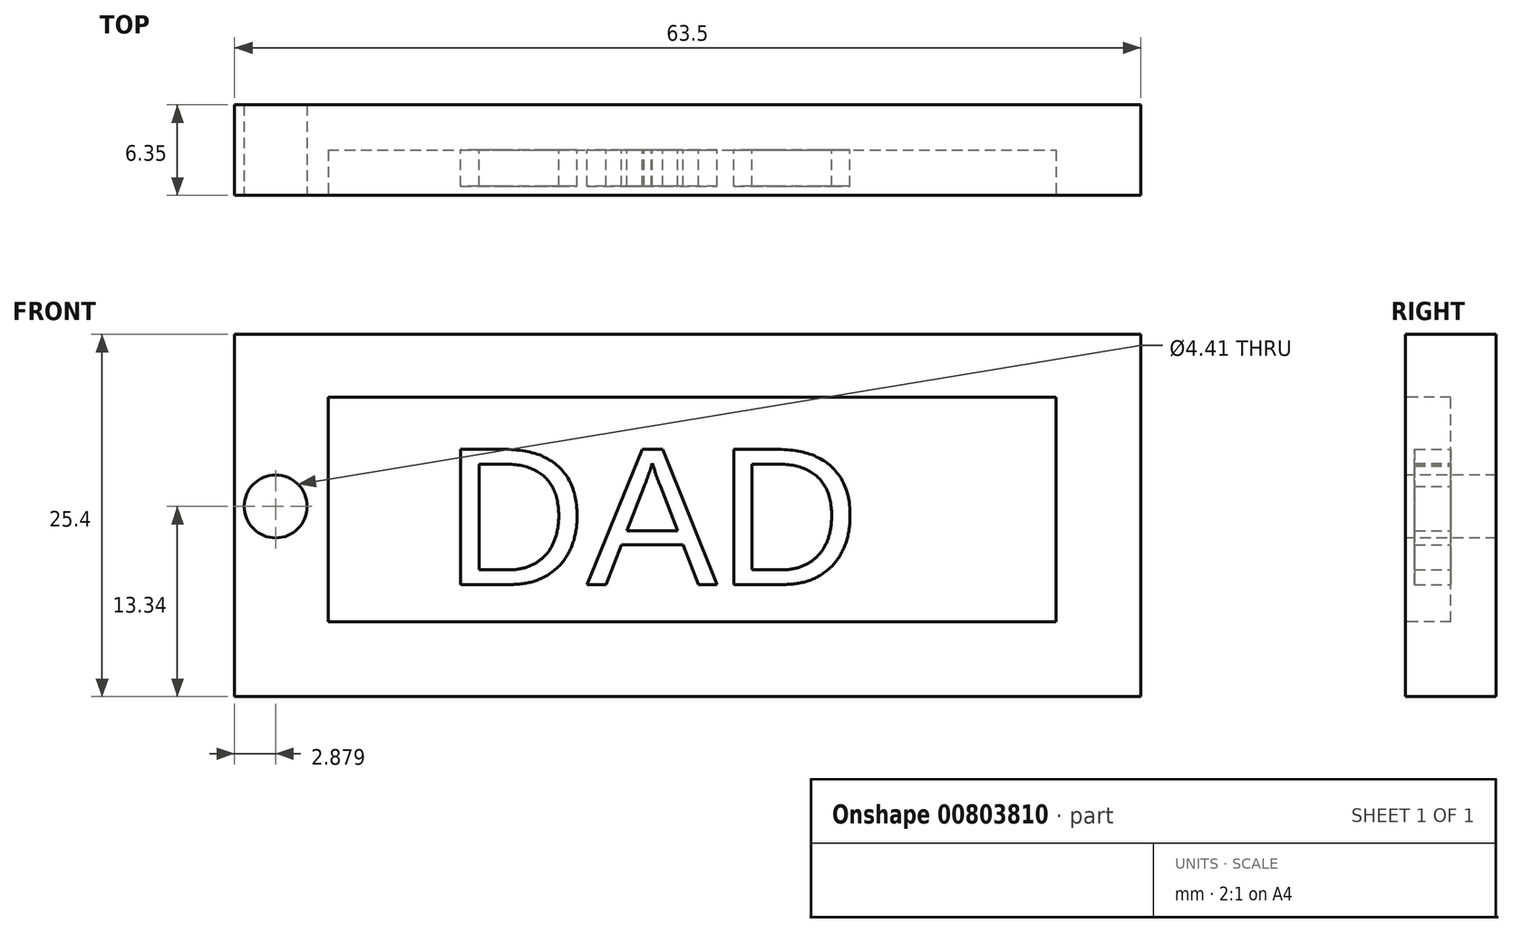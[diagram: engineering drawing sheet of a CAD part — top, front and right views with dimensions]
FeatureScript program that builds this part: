
annotation { "Feature Type Name" : "Feature", "Feature Type Description" : "" }
export const myFeature = defineFeature(function(context is Context, id is Id, definition is map)
    precondition{}
    {
        {
            var Q0;
            Q0=qCreatedBy(makeId("Front.planeOp"),FACE);
            var sketch = newSketch(context, id + "F0", { "sketchPlane" : qUnion([Q0])});
            skLineSegment(sketch, "E0.bottom", {"start": v(0, 0) * mm, "end": v(63.5, 0) * mm});
            skLineSegment(sketch, "E0.top", {"start": v(0, 25.4) * mm, "end": v(63.5, 25.4) * mm});
            skLineSegment(sketch, "E0.left", {"start": v(0, 0) * mm, "end": v(0, 25.4) * mm});
            skLineSegment(sketch, "E0.right", {"start": v(63.5, 0) * mm, "end": v(63.5, 25.4) * mm});
            skSolve(sketch);
        }
        {
            var Q0;
            Q0=makeQuery(id+"F0.imprint","IMPRINT",FACE,{"disambiguationData":[TD([[makeQuery(id+"F0.imprint","IMPRINT",EDGE,{"derivedFrom":sQuery(id+"F0.wireOp",EDGE,"E0.bottom")}),1.0]])]});
            var sketch = newSketch(context, id + "F1", { "sketchPlane" : qUnion([Q0])});
            skSolve(sketch);
        }
        {
            var Q0;
            Q0 = qSketchRegion(id + "F1", true);
            var Q1;
            Q1=makeQuery(id+"F0.imprint","IMPRINT",FACE,{"disambiguationData":[TD([[makeQuery(id+"F0.imprint","IMPRINT",EDGE,{"derivedFrom":sQuery(id+"F0.wireOp",EDGE,"E0.bottom")}),1.0]])]});
            extrude(context, id + "F2", {"entities" : qUnion([Q0, Q1]), "depth" : 6.35 * mm, "offsetDistance" : 25.4 * mm});
        }
        {
            var Q0;
            Q0=makeQuery(id+"F2.opExtrude","CAP_FACE",FACE,{"disambiguationData":[OSD([sQuery(id+"F0.wireOp",EDGE,"E0.bottom"),sQuery(id+"F0.wireOp",EDGE,"E0.top"),sQuery(id+"F0.wireOp",EDGE,"E0.left"),sQuery(id+"F0.wireOp",EDGE,"E0.right")])],"isStart":false});
            var sketch = newSketch(context, id + "F3", { "sketchPlane" : qUnion([Q0])});
            skLineSegment(sketch, "E1.bottom", {"start": v(6.56, 5.25) * mm, "end": v(57.57, 5.25) * mm});
            skLineSegment(sketch, "E1.top", {"start": v(6.56, 20.99) * mm, "end": v(57.57, 20.99) * mm});
            skLineSegment(sketch, "E1.left", {"start": v(6.56, 5.25) * mm, "end": v(6.56, 20.99) * mm});
            skLineSegment(sketch, "E1.right", {"start": v(57.57, 5.25) * mm, "end": v(57.57, 20.99) * mm});
            skSolve(sketch);
        }
        {
            var Q0;
            Q0=makeQuery(id+"F3.imprint","IMPRINT",FACE,{"disambiguationData":[TD([[makeQuery(id+"F3.imprint","IMPRINT",EDGE,{"derivedFrom":sQuery(id+"F3.wireOp",EDGE,"E1.bottom")}),1.0]])]});
            extrude(context, id + "F4", {"entities" : qUnion([Q0]), "operationType" : NewBodyOperationType.REMOVE, "oppositeDirection" : true, "depth" : 3.17 * mm, "offsetDistance" : 25.4 * mm});
        }
        {
            var Q0;
            Q0=qCreatedBy(makeId("Front.planeOp"),FACE);
            var sketch = newSketch(context, id + "F5", { "sketchPlane" : qUnion([Q0])});
            skCircle(sketch, "E2", {"center": v(2.88, 13.34) * mm, "radius": 2.2 * mm});
            skSolve(sketch);
        }
        {
            var Q0;
            Q0 = qSketchRegion(id + "F5", true);
            extrude(context, id + "F6", {"entities" : qUnion([Q0]), "operationType" : NewBodyOperationType.REMOVE, "oppositeDirection" : true, "depth" : 25.4 * mm, "offsetDistance" : 25.4 * mm, "symmetric" : true});
        }
        {
            var Q0;
            Q0=makeQuery(id+"F4.boolean.opBoolean","COPY",FACE,{"derivedFrom":makeQuery(id+"F4.opExtrude","CAP_FACE",FACE,{"disambiguationData":[OSD([sQuery(id+"F3.wireOp",EDGE,"E1.bottom"),sQuery(id+"F3.wireOp",EDGE,"E1.top"),sQuery(id+"F3.wireOp",EDGE,"E1.left"),sQuery(id+"F3.wireOp",EDGE,"E1.right")])],"isStart":false})});
            var sketch = newSketch(context, id + "F7", { "sketchPlane" : qUnion([Q0])});
            skText(sketch, "E3", { "text": "DAD", "fontName": "Arimo-Regular.ttf"});
            const initialGuessF7  = {"E3": [0.01472, 0.00787, 1, 0, 0.00991]};
            skSetInitialGuess(sketch, initialGuessF7);
            skSolve(sketch);
        }
        {
            var Q0;
            Q0 = qSketchRegion(id + "F7", true);
            extrude(context, id + "F8", {"entities" : qUnion([Q0]), "operationType" : NewBodyOperationType.ADD, "depth" : 2.54 * mm, "offsetDistance" : 25.4 * mm});
        }
    });
